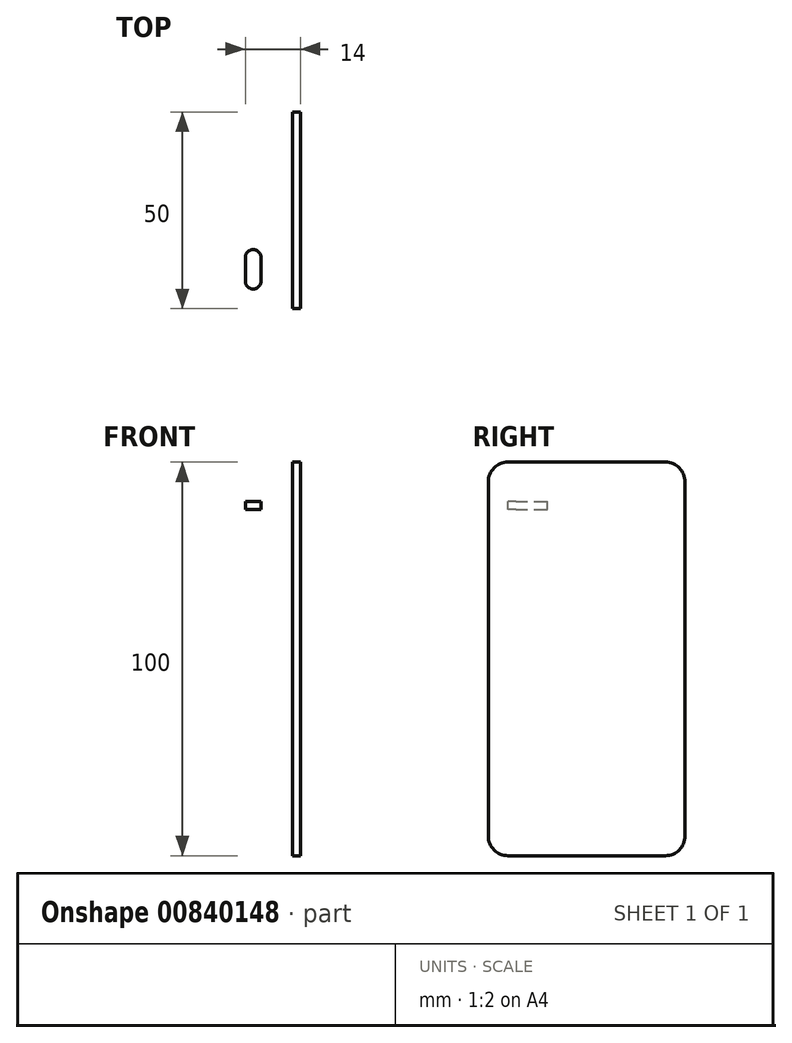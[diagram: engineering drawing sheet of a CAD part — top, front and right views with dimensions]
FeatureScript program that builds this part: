
annotation { "Feature Type Name" : "Feature", "Feature Type Description" : "" }
export const myFeature = defineFeature(function(context is Context, id is Id, definition is map)
    precondition{}
    {
        {
            var Q0;
            Q0=qCreatedBy(makeId("Front.planeOp"),FACE);
            var sketch = newSketch(context, id + "F0", { "sketchPlane" : qUnion([Q0])});
            skLineSegment(sketch, "E0.top", {"start": v(0, -2) * mm, "end": v(20, -2) * mm});
            skLineSegment(sketch, "E0.left", {"start": v(0, 0) * mm, "end": v(0, -2) * mm});
            skLineSegment(sketch, "E1.trimOffspring", {"start": v(0, 0) * mm, "end": v(20, 0) * mm});
            skLineSegment(sketch, "E2.bottom", {"start": v(22, 10) * mm, "end": v(20, 10) * mm});
            skLineSegment(sketch, "E2.top", {"start": v(22, -90) * mm, "end": v(20, -90) * mm});
            skLineSegment(sketch, "E2.right", {"start": v(20, 10) * mm, "end": v(20, 0) * mm});
            skLineSegment(sketch, "E3.trimOffspring", {"start": v(20, -2) * mm, "end": v(20, -90) * mm});
            skLineSegment(sketch, "E4.trimOffspring", {"start": v(22, 10) * mm, "end": v(22, -90) * mm});
            skSolve(sketch);
        }
        {
            var Q0;
            Q0=makeQuery(id+"F0.imprint","IMPRINT",FACE,{"disambiguationData":[TD([[makeQuery(id+"F0.imprint","IMPRINT",EDGE,{"derivedFrom":sQuery(id+"F0.wireOp",EDGE,"yEFS5gHq-5pEX-7EkC-DRV7-gzYHsLdJxijU.bottom")}),-1.0]])]});
            var Q1;
            Q1=makeQuery(id+"F0.imprint","IMPRINT",FACE,{"disambiguationData":[TD([[makeQuery(id+"F0.imprint","IMPRINT",EDGE,{"derivedFrom":sQuery(id+"F0.wireOp",EDGE,"E0.top")}),1.0]])]});
            extrude(context, id + "F1", {"entities" : qUnion([Q0, Q1]), "depth" : 50 * mm, "offsetDistance" : 25 * mm});
        }
        {
            var Q0;
            Q0=makeQuery(id+"F1.opExtrude","SWEPT_FACE",FACE,{"disambiguationData":[OSD([sQuery(id+"F0.wireOp",EDGE,"E1.trimOffspring")])]});
            var sketch = newSketch(context, id + "F2", { "sketchPlane" : qUnion([Q0])});
            skLineSegment(sketch, "E5.bottom", {"start": v(8, -7) * mm, "end": v(12, -7) * mm, "construction": true});
            skLineSegment(sketch, "E5.top", {"start": v(8, -13) * mm, "end": v(12, -13) * mm, "construction": true});
            skLineSegment(sketch, "E5.left", {"start": v(8, -7) * mm, "end": v(8, -13) * mm});
            skLineSegment(sketch, "E5.right", {"start": v(12, -7) * mm, "end": v(12, -13) * mm});
            skArc(sketch, "E6", {"start": v(12, -7) * mm, "mid": v(10, -5) * mm, "end": v(8, -7) * mm});
            skArc(sketch, "E7", {"start": v(8, -13) * mm, "mid": v(10, -15) * mm, "end": v(12, -13) * mm});
            skLineSegment(sketch, "E8", {"start": v(10, 0) * mm, "end": v(10, -50) * mm, "construction": true});
            skLineSegment(sketch, "E9", {"start": v(0, -25) * mm, "end": v(20, -25) * mm, "construction": true});
            skArc(sketch, "E10.MirrorCS", {"start": v(12, -43) * mm, "mid": v(10, -45) * mm, "end": v(8, -43) * mm});
            skLineSegment(sketch, "E11.MirrorCS", {"start": v(8, -43) * mm, "end": v(12, -43) * mm, "construction": true});
            skLineSegment(sketch, "E12.MirrorCS", {"start": v(8, -37) * mm, "end": v(12, -37) * mm, "construction": true});
            skArc(sketch, "E13.MirrorCS", {"start": v(8, -37) * mm, "mid": v(10, -35) * mm, "end": v(12, -37) * mm});
            skLineSegment(sketch, "E14.MirrorCS", {"start": v(12, -43) * mm, "end": v(12, -37) * mm});
            skLineSegment(sketch, "E15.MirrorCS", {"start": v(8, -43) * mm, "end": v(8, -37) * mm});
            skSolve(sketch);
        }
        {
            var Q0;
            Q0=makeQuery(id+"F2.imprint","IMPRINT",FACE,{"disambiguationData":[TD([[makeQuery(id+"F2.imprint","IMPRINT",EDGE,{"derivedFrom":sQuery(id+"F2.wireOp",EDGE,"E5.left")}),1.0]])]});
            var Q1;
            Q1=makeQuery(id+"F2.imprint","IMPRINT",FACE,{"disambiguationData":[TD([[makeQuery(id+"F2.imprint","IMPRINT",EDGE,{"derivedFrom":sQuery(id+"F2.wireOp",EDGE,"E10.MirrorCS")}),-1.0]])]});
            extrude(context, id + "F3", {"entities" : qUnion([Q0, Q1]), "operationType" : NewBodyOperationType.REMOVE, "oppositeDirection" : true, "depth" : 25 * mm, "offsetDistance" : 25 * mm});
        }
        {
            var Q0;
            Q0=makeQuery(id+"F1.opExtrude","CAP_EDGE",EDGE,{"disambiguationData":[OSD([sQuery(id+"F0.wireOp",EDGE,"E2.bottom")])],"isStart":false});
            var Q1;
            Q1=makeQuery(id+"F1.opExtrude","CAP_EDGE",EDGE,{"disambiguationData":[OSD([sQuery(id+"F0.wireOp",EDGE,"E2.bottom")])],"isStart":true});
            var Q2;
            Q2=makeQuery(id+"F1.opExtrude","CAP_EDGE",EDGE,{"disambiguationData":[OSD([sQuery(id+"F0.wireOp",EDGE,"E2.top")])],"isStart":false});
            var Q3;
            Q3=makeQuery(id+"F1.opExtrude","CAP_EDGE",EDGE,{"disambiguationData":[OSD([sQuery(id+"F0.wireOp",EDGE,"E2.top")])],"isStart":true});
            var Q4;
            Q4=makeQuery(id+"F1.opExtrude","CAP_EDGE",EDGE,{"disambiguationData":[OSD([sQuery(id+"F0.wireOp",EDGE,"E0.left")])],"isStart":false});
            var Q5;
            Q5=makeQuery(id+"F1.opExtrude","CAP_EDGE",EDGE,{"disambiguationData":[OSD([sQuery(id+"F0.wireOp",EDGE,"E0.left")])],"isStart":true});
            fillet(context, id + "F4", {"entities" : qUnion([Q0, Q1, Q2, Q3, Q4, Q5]), "radius" : 5 * mm, "tangentPropagation" : true, "allowEdgeOverflow" : false});
        }
    });
